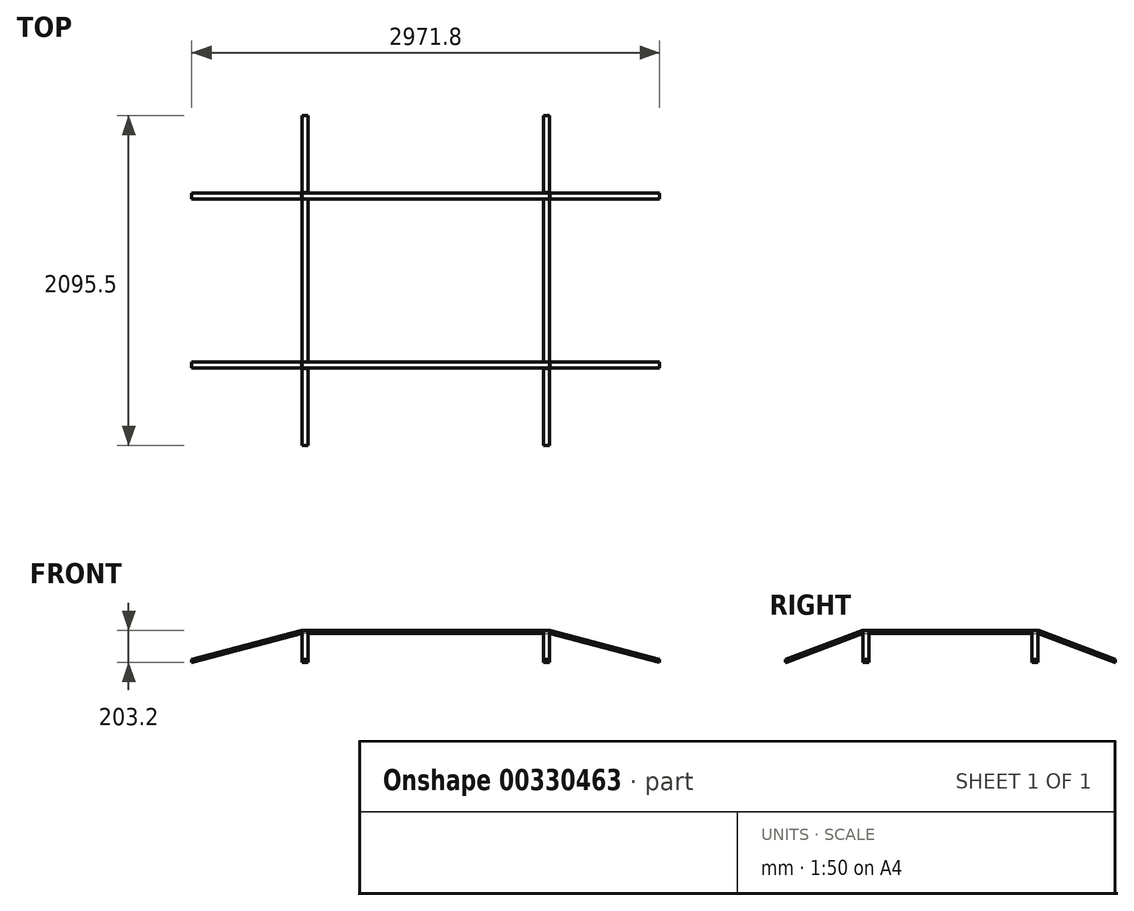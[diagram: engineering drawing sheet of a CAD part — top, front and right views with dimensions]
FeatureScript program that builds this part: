
annotation { "Feature Type Name" : "Feature", "Feature Type Description" : "" }
export const myFeature = defineFeature(function(context is Context, id is Id, definition is map)
    precondition{}
    {
        {
            var Q0;
            Q0=qCreatedBy(makeId("Top.planeOp"),FACE);
            var sketch = newSketch(context, id + "F0", { "sketchPlane" : qUnion([Q0])});
            skLineSegment(sketch, "E0.bottom", {"start": v(-786.66, 555.78) * mm, "end": v(786.66, 555.78) * mm});
            skLineSegment(sketch, "E0.top", {"start": v(-786.66, -555.78) * mm, "end": v(786.66, -555.78) * mm, "construction": true});
            skLineSegment(sketch, "E0.left", {"start": v(-786.66, 555.78) * mm, "end": v(-786.66, -555.78) * mm, "construction": true});
            skLineSegment(sketch, "E0.right", {"start": v(786.66, 555.78) * mm, "end": v(786.66, -555.78) * mm, "construction": true});
            skPoint(sketch, "E0.middle", {"position": v(0, 0) * mm});
            skLineSegment(sketch, "E1.0", {"start": v(748.56, 517.68) * mm, "end": v(748.56, -517.68) * mm, "construction": true});
            skLineSegment(sketch, "E1.1", {"start": v(-748.56, 517.68) * mm, "end": v(748.56, 517.68) * mm, "construction": true});
            skLineSegment(sketch, "E1.2", {"start": v(-748.56, 517.68) * mm, "end": v(-748.56, -517.68) * mm, "construction": true});
            skLineSegment(sketch, "E1.3", {"start": v(-748.56, -517.68) * mm, "end": v(748.56, -517.68) * mm, "construction": true});
            skLineSegment(sketch, "E2", {"start": v(-786.66, 517.68) * mm, "end": v(786.66, 517.68) * mm});
            skLineSegment(sketch, "E3", {"start": v(786.66, 555.78) * mm, "end": v(786.66, 517.68) * mm});
            skLineSegment(sketch, "E4", {"start": v(-786.66, 555.78) * mm, "end": v(-786.66, 517.68) * mm});
            skSolve(sketch);
        }
        {
            var Q0;
            Q0=makeQuery(id+"F0.imprint","IMPRINT",FACE,{"disambiguationData":[TD([[makeQuery(id+"F0.imprint","IMPRINT",EDGE,{"derivedFrom":sQuery(id+"F0.wireOp",EDGE,"E0.bottom")}),-1.0]])]});
            extrude(context, id + "F1", {"entities" : qUnion([Q0]), "oppositeDirection" : true, "depth" : 19.05 * mm});
        }
        {
            var Q0;
            Q0=qCreatedBy(makeId("Top.planeOp"),FACE);
            var sketch = newSketch(context, id + "F2", { "sketchPlane" : qUnion([Q0])});
            skLineSegment(sketch, "E5.bottom", {"start": v(-786.66, 555.78) * mm, "end": v(786.66, 555.78) * mm, "construction": true});
            skLineSegment(sketch, "E5.top", {"start": v(-786.66, -555.78) * mm, "end": v(786.66, -555.78) * mm, "construction": true});
            skLineSegment(sketch, "E5.left", {"start": v(-786.66, 555.78) * mm, "end": v(-786.66, -555.78) * mm, "construction": true});
            skLineSegment(sketch, "E5.right", {"start": v(786.66, 555.78) * mm, "end": v(786.66, -555.78) * mm, "construction": true});
            skPoint(sketch, "E5.middle", {"position": v(0, 0) * mm});
            skLineSegment(sketch, "E6.0", {"start": v(748.56, 517.68) * mm, "end": v(748.56, -517.68) * mm, "construction": true});
            skLineSegment(sketch, "E6.1", {"start": v(-748.56, 517.68) * mm, "end": v(748.56, 517.68) * mm, "construction": true});
            skLineSegment(sketch, "E6.2", {"start": v(-748.56, 517.68) * mm, "end": v(-748.56, -517.68) * mm, "construction": true});
            skLineSegment(sketch, "E6.3", {"start": v(-748.56, -517.68) * mm, "end": v(748.56, -517.68) * mm, "construction": true});
            skLineSegment(sketch, "E7", {"start": v(748.56, 517.68) * mm, "end": v(786.66, 517.68) * mm});
            skLineSegment(sketch, "E8", {"start": v(786.66, 517.68) * mm, "end": v(786.66, -517.68) * mm});
            skLineSegment(sketch, "E9", {"start": v(786.66, -517.68) * mm, "end": v(748.56, -517.68) * mm});
            skLineSegment(sketch, "E10", {"start": v(748.56, -517.68) * mm, "end": v(748.56, 517.68) * mm});
            skSolve(sketch);
        }
        {
            var Q0;
            Q0=makeQuery(id+"F2.imprint","IMPRINT",FACE,{"disambiguationData":[TD([[makeQuery(id+"F2.imprint","IMPRINT",EDGE,{"derivedFrom":sQuery(id+"F2.wireOp",EDGE,"E7")}),-1.0]])]});
            extrude(context, id + "F3", {"entities" : qUnion([Q0]), "oppositeDirection" : true, "depth" : 19.05 * mm});
        }
        {
            var Q0;
            Q0=makeQuery(id+"F1.opExtrude","SWEPT_BODY",BODY,{"disambiguationData":[OSD([sQuery(id+"F0.wireOp",EDGE,"E0.bottom"),sQuery(id+"F0.wireOp",EDGE,"E2"),sQuery(id+"F0.wireOp",EDGE,"E3"),sQuery(id+"F0.wireOp",EDGE,"E4")])]});
            var Q1;
            Q1=qCreatedBy(makeId("Front.planeOp"),FACE);
            mirror(context, id + "F4", {"entities" : qUnion([Q0]), "mirrorPlane" : qUnion([Q1])});
        }
        {
            var Q0;
            Q0=makeQuery(id+"F3.opExtrude","SWEPT_BODY",BODY,{"disambiguationData":[OSD([sQuery(id+"F2.wireOp",EDGE,"E7"),sQuery(id+"F2.wireOp",EDGE,"E8"),sQuery(id+"F2.wireOp",EDGE,"E9"),sQuery(id+"F2.wireOp",EDGE,"E10")])]});
            var Q1;
            Q1=qCreatedBy(makeId("Right.planeOp"),FACE);
            mirror(context, id + "F5", {"entities" : qUnion([Q0]), "mirrorPlane" : qUnion([Q1])});
        }
        {
            var Q0;
            Q0=makeQuery(id+"F1.opExtrude","SWEPT_FACE",FACE,{"disambiguationData":[OSD([sQuery(id+"F0.wireOp",EDGE,"E3")])]});
            var sketch = newSketch(context, id + "F6", { "sketchPlane" : qUnion([Q0])});
            skLineSegment(sketch, "E11", {"start": v(555.78, -19.05) * mm, "end": v(1044.28, -203.2) * mm});
            skLineSegment(sketch, "E12", {"start": v(1044.28, -203.2) * mm, "end": v(1098.28, -203.2) * mm});
            skLineSegment(sketch, "E13", {"start": v(1098.28, -203.2) * mm, "end": v(555.78, 1.3) * mm});
            skLineSegment(sketch, "E14", {"start": v(555.78, 1.3) * mm, "end": v(555.78, -19.05) * mm});
            skLineSegment(sketch, "E15", {"start": v(555.78, 0) * mm, "end": v(559.25, 0) * mm});
            skLineSegment(sketch, "E16", {"start": v(1047.75, -203.2) * mm, "end": v(1047.75, -184.15) * mm});
            skPoint(sketch, "E17", {"position": v(1071.28, -203.2) * mm});
            skSolve(sketch);
        }
        {
            var Q0;
            {var subQ3=sQuery(id+"F6.wireOp",EDGE,"E11");Q0=makeQuery(id+"F6.imprint","IMPRINT",FACE,{"disambiguationData":[TD([[makeQuery(id+"F6.imprint","IMPRINT",EDGE,{"derivedFrom":subQ3}),1.0]])]});}
            extrude(context, id + "F7", {"entities" : qUnion([Q0]), "oppositeDirection" : true, "depth" : 38.1 * mm});
        }
        {
            var Q0;
            Q0=makeQuery(id+"F7.opExtrude","SWEPT_BODY",BODY,{"disambiguationData":[OSD([sQuery(id+"F6.wireOp",EDGE,"E11"),sQuery(id+"F6.wireOp",EDGE,"E12"),sQuery(id+"F6.wireOp",EDGE,"E13"),sQuery(id+"F6.wireOp",EDGE,"E14"),sQuery(id+"F6.wireOp",EDGE,"E15"),sQuery(id+"F6.wireOp",EDGE,"E16")])]});
            var Q1;
            Q1=qCreatedBy(makeId("Right.planeOp"),FACE);
            mirror(context, id + "F8", {"entities" : qUnion([Q0]), "mirrorPlane" : qUnion([Q1])});
        }
        {
            var Q0;
            Q0=makeQuery(id+"F8.opPattern","COPY",BODY,{"derivedFrom":makeQuery(id+"F7.opExtrude","SWEPT_BODY",BODY,{"disambiguationData":[OSD([sQuery(id+"F6.wireOp",EDGE,"E11"),sQuery(id+"F6.wireOp",EDGE,"E12"),sQuery(id+"F6.wireOp",EDGE,"E13"),sQuery(id+"F6.wireOp",EDGE,"E14"),sQuery(id+"F6.wireOp",EDGE,"E15"),sQuery(id+"F6.wireOp",EDGE,"E16")])]}),"instanceName":"1"});
            var Q1;
            Q1=makeQuery(id+"F7.opExtrude","SWEPT_BODY",BODY,{"disambiguationData":[OSD([sQuery(id+"F6.wireOp",EDGE,"E11"),sQuery(id+"F6.wireOp",EDGE,"E12"),sQuery(id+"F6.wireOp",EDGE,"E13"),sQuery(id+"F6.wireOp",EDGE,"E14"),sQuery(id+"F6.wireOp",EDGE,"E15"),sQuery(id+"F6.wireOp",EDGE,"E16")])]});
            var Q2;
            Q2=qCreatedBy(makeId("Front.planeOp"),FACE);
            mirror(context, id + "F9", {"entities" : qUnion([Q0, Q1]), "mirrorPlane" : qUnion([Q2])});
        }
        {
            var Q0;
            Q0=makeQuery(id+"F1.opExtrude","SWEPT_FACE",FACE,{"disambiguationData":[OSD([sQuery(id+"F0.wireOp",EDGE,"E0.bottom")])]});
            var sketch = newSketch(context, id + "F10", { "sketchPlane" : qUnion([Q0])});
            skLineSegment(sketch, "E18", {"start": v(-786.66, 0.65) * mm, "end": v(-1557.98, -203.2) * mm});
            skLineSegment(sketch, "E19", {"start": v(-1557.98, -203.2) * mm, "end": v(-1483.43, -203.2) * mm});
            skLineSegment(sketch, "E20", {"start": v(-1483.43, -203.2) * mm, "end": v(-786.66, -19.05) * mm});
            skLineSegment(sketch, "E21", {"start": v(-786.66, 0.65) * mm, "end": v(-786.66, -19.05) * mm});
            skPoint(sketch, "E22", {"position": v(-1520.7, -203.2) * mm});
            skLineSegment(sketch, "E23", {"start": v(-1485.9, -184.15) * mm, "end": v(-1485.9, -203.2) * mm});
            skLineSegment(sketch, "E24.0.0", {"start": v(-786.66, 0) * mm, "end": v(-786.66, -184.15) * mm, "construction": true});
            skLineSegment(sketch, "E25", {"start": v(-786.66, 0) * mm, "end": v(-789.14, 0) * mm});
            skSolve(sketch);
        }
        {
            var Q0;
            {var subQ3=sQuery(id+"F10.wireOp",EDGE,"E20");Q0=makeQuery(id+"F10.imprint","IMPRINT",FACE,{"disambiguationData":[TD([[makeQuery(id+"F10.imprint","IMPRINT",EDGE,{"derivedFrom":subQ3}),1.0]])]});}
            extrude(context, id + "F11", {"entities" : qUnion([Q0]), "oppositeDirection" : true, "depth" : 38.1 * mm});
        }
        {
            var Q0;
            Q0=makeQuery(id+"F11.opExtrude","SWEPT_BODY",BODY,{"disambiguationData":[OSD([sQuery(id+"F10.wireOp",EDGE,"E18"),sQuery(id+"F10.wireOp",EDGE,"E19"),sQuery(id+"F10.wireOp",EDGE,"E20"),sQuery(id+"F10.wireOp",EDGE,"E21"),sQuery(id+"F10.wireOp",EDGE,"E23"),sQuery(id+"F10.wireOp",EDGE,"E25")])]});
            var Q1;
            Q1=qCreatedBy(makeId("Front.planeOp"),FACE);
            mirror(context, id + "F12", {"entities" : qUnion([Q0]), "mirrorPlane" : qUnion([Q1])});
        }
        {
            var Q0;
            Q0=makeQuery(id+"F12.opPattern","COPY",BODY,{"derivedFrom":makeQuery(id+"F11.opExtrude","SWEPT_BODY",BODY,{"disambiguationData":[OSD([sQuery(id+"F10.wireOp",EDGE,"E18"),sQuery(id+"F10.wireOp",EDGE,"E19"),sQuery(id+"F10.wireOp",EDGE,"E20"),sQuery(id+"F10.wireOp",EDGE,"E21"),sQuery(id+"F10.wireOp",EDGE,"E23"),sQuery(id+"F10.wireOp",EDGE,"E25")])]}),"instanceName":"1"});
            var Q1;
            Q1=makeQuery(id+"F11.opExtrude","SWEPT_BODY",BODY,{"disambiguationData":[OSD([sQuery(id+"F10.wireOp",EDGE,"E18"),sQuery(id+"F10.wireOp",EDGE,"E19"),sQuery(id+"F10.wireOp",EDGE,"E20"),sQuery(id+"F10.wireOp",EDGE,"E21"),sQuery(id+"F10.wireOp",EDGE,"E23"),sQuery(id+"F10.wireOp",EDGE,"E25")])]});
            var Q2;
            Q2=qCreatedBy(makeId("Right.planeOp"),FACE);
            mirror(context, id + "F13", {"entities" : qUnion([Q0, Q1]), "mirrorPlane" : qUnion([Q2])});
        }
    });
